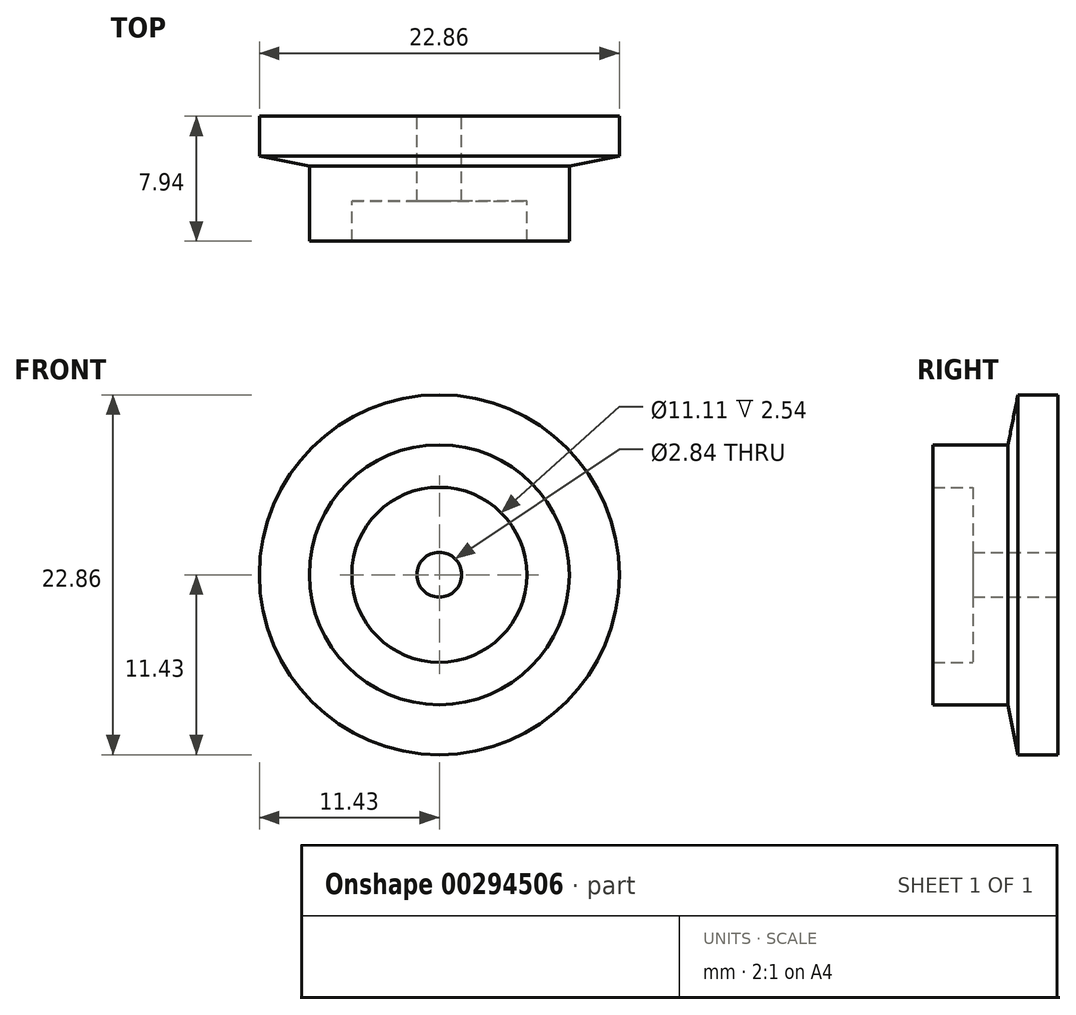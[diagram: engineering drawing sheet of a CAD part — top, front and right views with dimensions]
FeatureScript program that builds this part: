
annotation { "Feature Type Name" : "Feature", "Feature Type Description" : "" }
export const myFeature = defineFeature(function(context is Context, id is Id, definition is map)
    precondition{}
    {
        {
            var Q0;
            Q0=qCreatedBy(makeId("Right.planeOp"),FACE);
            var sketch = newSketch(context, id + "F0", { "sketchPlane" : qUnion([Q0])});
            skLineSegment(sketch, "E0", {"start": v(0, 5.56) * mm, "end": v(0, 8.26) * mm});
            skLineSegment(sketch, "E1", {"start": v(0, 8.26) * mm, "end": v(4.76, 8.26) * mm});
            skLineSegment(sketch, "E2", {"start": v(4.76, 8.26) * mm, "end": v(5.4, 11.43) * mm});
            skLineSegment(sketch, "E3", {"start": v(2.54, 1.42) * mm, "end": v(7.94, 1.42) * mm});
            skLineSegment(sketch, "E4", {"start": v(7.94, 0) * mm, "end": v(0, 0) * mm, "construction": true});
            skLineSegment(sketch, "E5", {"start": v(5.4, 11.43) * mm, "end": v(7.94, 11.43) * mm});
            skLineSegment(sketch, "E6", {"start": v(7.94, 11.43) * mm, "end": v(7.94, 1.42) * mm});
            skPoint(sketch, "E7.orphan", {"position": v(7.94, 1.42) * mm});
            skLineSegment(sketch, "E8.top", {"start": v(0, 5.56) * mm, "end": v(2.54, 5.56) * mm});
            skLineSegment(sketch, "E8.right", {"start": v(2.54, 1.42) * mm, "end": v(2.54, 5.56) * mm});
            skPoint(sketch, "E9.orphan", {"position": v(0, 1.42) * mm});
            skSolve(sketch);
        }
        {
            var Q0;
            Q0=makeQuery(id+"F0.imprint","IMPRINT",FACE,{"disambiguationData":[TD([[makeQuery(id+"F0.imprint","IMPRINT",EDGE,{"derivedFrom":sQuery(id+"F0.wireOp",EDGE,"E0")}),-1.0]])]});
            var Q1;
            Q1=sQuery(id+"F0.wireOp",EDGE,"E4");
            revolve(context, id + "F1", {"entities" : qUnion([Q0]), "axis" : qUnion([Q1]), "revolveType" : RevolveType.FULL});
        }
    });
